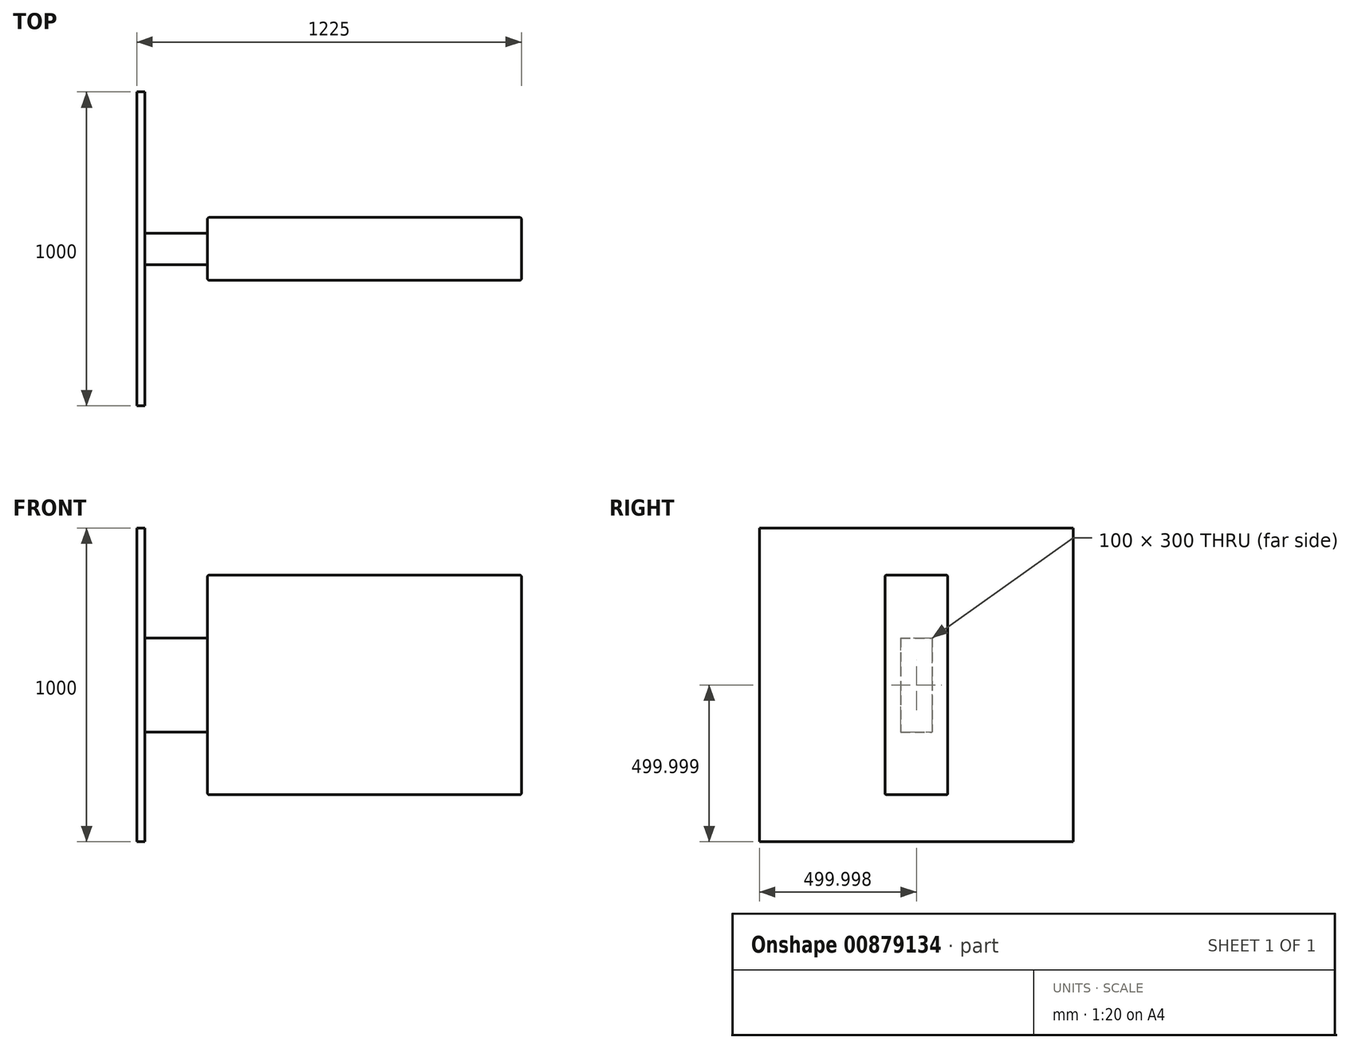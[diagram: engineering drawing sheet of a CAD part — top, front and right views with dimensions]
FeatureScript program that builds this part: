
annotation { "Feature Type Name" : "Feature", "Feature Type Description" : "" }
export const myFeature = defineFeature(function(context is Context, id is Id, definition is map)
    precondition{}
    {
        {
            var Q0;
            Q0=qCreatedBy(makeId("Right.planeOp"),FACE);
            var sketch = newSketch(context, id + "F0", { "sketchPlane" : qUnion([Q0])});
            skLineSegment(sketch, "E0.bottom", {"start": v(-165.1, 927.16) * mm, "end": v(834.9, 927.16) * mm});
            skLineSegment(sketch, "E0.top", {"start": v(-165.1, -72.84) * mm, "end": v(834.9, -72.84) * mm});
            skLineSegment(sketch, "E0.left", {"start": v(-165.1, 927.16) * mm, "end": v(-165.1, -72.84) * mm});
            skLineSegment(sketch, "E0.right", {"start": v(834.9, 927.16) * mm, "end": v(834.9, -72.84) * mm});
            skSolve(sketch);
        }
        {
            var Q0;
            Q0=makeQuery(id+"F0.imprint","IMPRINT",FACE,{"disambiguationData":[TD([[makeQuery(id+"F0.imprint","IMPRINT",EDGE,{"derivedFrom":sQuery(id+"F0.wireOp",EDGE,"E0.bottom")}),-1.0]])]});
            extrude(context, id + "F1", {"entities" : qUnion([Q0]), "depth" : 25 * mm, "offsetDistance" : 25 * mm});
        }
        {
            var Q0;
            Q0=makeQuery(id+"F1.opExtrude","CAP_FACE",FACE,{"disambiguationData":[OSD([sQuery(id+"F0.wireOp",EDGE,"E0.bottom"),sQuery(id+"F0.wireOp",EDGE,"E0.top"),sQuery(id+"F0.wireOp",EDGE,"E0.left"),sQuery(id+"F0.wireOp",EDGE,"E0.right")])],"isStart":false});
            var sketch = newSketch(context, id + "F2", { "sketchPlane" : qUnion([Q0])});
            skLineSegment(sketch, "E1.bottom", {"start": v(284.9, 577.16) * mm, "end": v(384.9, 577.16) * mm});
            skLineSegment(sketch, "E1.top", {"start": v(284.9, 277.16) * mm, "end": v(384.9, 277.16) * mm});
            skLineSegment(sketch, "E1.left", {"start": v(284.9, 577.16) * mm, "end": v(284.9, 277.16) * mm});
            skLineSegment(sketch, "E1.right", {"start": v(384.9, 577.16) * mm, "end": v(384.9, 277.16) * mm});
            skSolve(sketch);
        }
        {
            var Q0;
            Q0 = qSketchRegion(id + "F2", true);
            var Q1;
            Q1=makeQuery(id+"F2.imprint","IMPRINT",FACE,{"disambiguationData":[TD([[makeQuery(id+"F2.imprint","IMPRINT",EDGE,{"derivedFrom":sQuery(id+"F2.wireOp",EDGE,"E1.bottom")}),-1.0]])]});
            extrude(context, id + "F3", {"entities" : qUnion([Q0, Q1]), "operationType" : NewBodyOperationType.ADD, "depth" : 200 * mm, "offsetDistance" : 25 * mm});
        }
        {
            var Q0;
            Q0=makeQuery(id+"F3.opExtrude","CAP_FACE",FACE,{"disambiguationData":[OSD([sQuery(id+"F2.wireOp",EDGE,"E1.bottom"),sQuery(id+"F2.wireOp",EDGE,"E1.top"),sQuery(id+"F2.wireOp",EDGE,"E1.left"),sQuery(id+"F2.wireOp",EDGE,"E1.right")])],"isStart":false});
            var sketch = newSketch(context, id + "F4", { "sketchPlane" : qUnion([Q0])});
            skLineSegment(sketch, "E2.bottom", {"start": v(234.9, 777.16) * mm, "end": v(434.9, 777.16) * mm});
            skLineSegment(sketch, "E2.top", {"start": v(234.9, 77.16) * mm, "end": v(434.9, 77.16) * mm});
            skLineSegment(sketch, "E2.left", {"start": v(234.9, 777.16) * mm, "end": v(234.9, 77.16) * mm});
            skLineSegment(sketch, "E2.right", {"start": v(434.9, 777.16) * mm, "end": v(434.9, 77.16) * mm});
            skSolve(sketch);
        }
        {
            var Q0;
            Q0=makeQuery(id+"F4.imprint","IMPRINT",FACE,{"disambiguationData":[TD([[makeQuery(id+"F4.imprint","IMPRINT",EDGE,{"derivedFrom":sQuery(id+"F4.wireOp",EDGE,"E2.bottom")}),-1.0]])]});
            var Q1;
            Q1=makeQuery(id+"F4.imprint","IMPRINT",FACE,{"disambiguationData":[TD([[makeQuery(id+"F4.imprint","IMPRINT",EDGE,{"derivedFrom":makeQuery(id+"F3.opExtrude","CAP_EDGE",EDGE,{"disambiguationData":[OSD([sQuery(id+"F2.wireOp",EDGE,"E1.bottom")])],"isStart":false})}),-1.0]])]});
            extrude(context, id + "F5", {"entities" : qUnion([Q0, Q1]), "operationType" : NewBodyOperationType.ADD, "depth" : 1000 * mm, "offsetDistance" : 25 * mm});
        }
        {
            var Q0;
            Q0=makeQuery(id+"F5.opExtrude","CAP_EDGE",EDGE,{"disambiguationData":[OSD([sQuery(id+"F4.wireOp",EDGE,"E2.left")])],"isStart":true});
            var Q1;
            Q1=makeQuery(id+"F3.opExtrude","CAP_EDGE",EDGE,{"disambiguationData":[OSD([sQuery(id+"F2.wireOp",EDGE,"E1.left")])],"isStart":false});
            var Q2;
            Q2=makeQuery(id+"F5.opExtrude","SWEPT_EDGE",EDGE,{"disambiguationData":[OSD([sQuery(id+"F4.wireOp",EDGE,"E2.bottom"),sQuery(id+"F4.wireOp",EDGE,"E2.left")])]});
            var Q3;
            Q3=makeQuery(id+"F5.opExtrude","CAP_EDGE",EDGE,{"disambiguationData":[OSD([sQuery(id+"F4.wireOp",EDGE,"E2.left")])],"isStart":false});
            var Q4;
            Q4=makeQuery(id+"F5.opExtrude","CAP_EDGE",EDGE,{"disambiguationData":[OSD([sQuery(id+"F4.wireOp",EDGE,"E2.bottom")])],"isStart":false});
            var Q5;
            {var subQ0=sQuery(id+"F4.wireOp",EDGE,"E2.right");Q5=makeQuery(id+"FXXYBiBw9IYmjL2_1.boolean.opBoolean","COPY",EDGE,{"derivedFrom":makeQuery(id+"FXXYBiBw9IYmjL2_1.opExtrude","CAP_EDGE",EDGE,{"disambiguationData":[OSD([subQ0]),TDD([makeQuery(id+"FunBPICaKllMgSO_1.imprint","IMPRINT",EDGE,{"derivedFrom":makeQuery(id+"F5.opExtrude","CAP_EDGE",EDGE,{"disambiguationData":[OSD([subQ0])],"isStart":false})})])],"isStart":false})});}
            var Q6;
            Q6=makeQuery(id+"F5.opExtrude","SWEPT_EDGE",EDGE,{"disambiguationData":[OSD([sQuery(id+"F4.wireOp",EDGE,"E2.top"),sQuery(id+"F4.wireOp",EDGE,"E2.left")])]});
            var Q7;
            Q7=makeQuery(id+"F5.opExtrude","CAP_EDGE",EDGE,{"disambiguationData":[OSD([sQuery(id+"F4.wireOp",EDGE,"E2.top")])],"isStart":true});
            var Q8;
            Q8=makeQuery(id+"FXXYBiBw9IYmjL2_1.boolean.opBoolean","COPY",EDGE,{"derivedFrom":makeQuery(id+"FXXYBiBw9IYmjL2_1.opExtrude","CAP_EDGE",EDGE,{"disambiguationData":[OSD([sQuery(id+"F4.wireOp",EDGE,"E2.top"),sQuery(id+"F4.wireOp",EDGE,"E2.right")])],"isStart":false})});
            var Q9;
            Q9=makeQuery(id+"F5.opExtrude","CAP_EDGE",EDGE,{"disambiguationData":[OSD([sQuery(id+"F4.wireOp",EDGE,"E2.top")])],"isStart":false});
            var Q10;
            Q10=makeQuery(id+"FXXYBiBw9IYmjL2_1.boolean.opBoolean","COPY",EDGE,{"derivedFrom":makeQuery(id+"FXXYBiBw9IYmjL2_1.opExtrude","CAP_EDGE",EDGE,{"disambiguationData":[OSD([sQuery(id+"F4.wireOp",EDGE,"E2.bottom"),sQuery(id+"F4.wireOp",EDGE,"E2.right")])],"isStart":false})});
            var Q11;
            Q11=makeQuery(id+"F5.opExtrude","CAP_EDGE",EDGE,{"disambiguationData":[OSD([sQuery(id+"F4.wireOp",EDGE,"E2.bottom")])],"isStart":true});
            var Q12;
            {var subQ0=sQuery(id+"F4.wireOp",EDGE,"E2.right");Q12=makeQuery(id+"FXXYBiBw9IYmjL2_1.boolean.opBoolean","COPY",EDGE,{"derivedFrom":makeQuery(id+"FXXYBiBw9IYmjL2_1.opExtrude","CAP_EDGE",EDGE,{"disambiguationData":[OSD([subQ0]),TDD([makeQuery(id+"FunBPICaKllMgSO_1.imprint","IMPRINT",EDGE,{"derivedFrom":makeQuery(id+"F5.opExtrude","CAP_EDGE",EDGE,{"disambiguationData":[OSD([subQ0])],"isStart":true})})])],"isStart":false})});}
            fillet(context, id + "F6", {"entities" : qUnion([Q0, Q1, Q2, Q3, Q4, Q5, Q6, Q7, Q8, Q9, Q10, Q11, Q12]), "radius" : 5 * mm, "tangentPropagation" : true, "allowEdgeOverflow" : false});
        }
        {
            var Q0;
            Q0=makeQuery(id+"F5.opExtrude","SWEPT_EDGE",EDGE,{"disambiguationData":[OSD([sQuery(id+"F4.wireOp",EDGE,"E2.bottom"),sQuery(id+"F4.wireOp",EDGE,"E2.right")])]});
            var Q1;
            Q1=makeQuery(id+"F5.opExtrude","CAP_EDGE",EDGE,{"disambiguationData":[OSD([sQuery(id+"F4.wireOp",EDGE,"E2.right")])],"isStart":false});
            var Q2;
            Q2=makeQuery(id+"F5.opExtrude","CAP_EDGE",EDGE,{"disambiguationData":[OSD([sQuery(id+"F4.wireOp",EDGE,"E2.right")])],"isStart":true});
            var Q3;
            Q3=makeQuery(id+"F5.opExtrude","SWEPT_EDGE",EDGE,{"disambiguationData":[OSD([sQuery(id+"F4.wireOp",EDGE,"E2.top"),sQuery(id+"F4.wireOp",EDGE,"E2.right")])]});
            fillet(context, id + "F7", {"entities" : qUnion([Q0, Q1, Q2, Q3]), "radius" : 5 * mm, "tangentPropagation" : true, "allowEdgeOverflow" : false});
        }
    });
